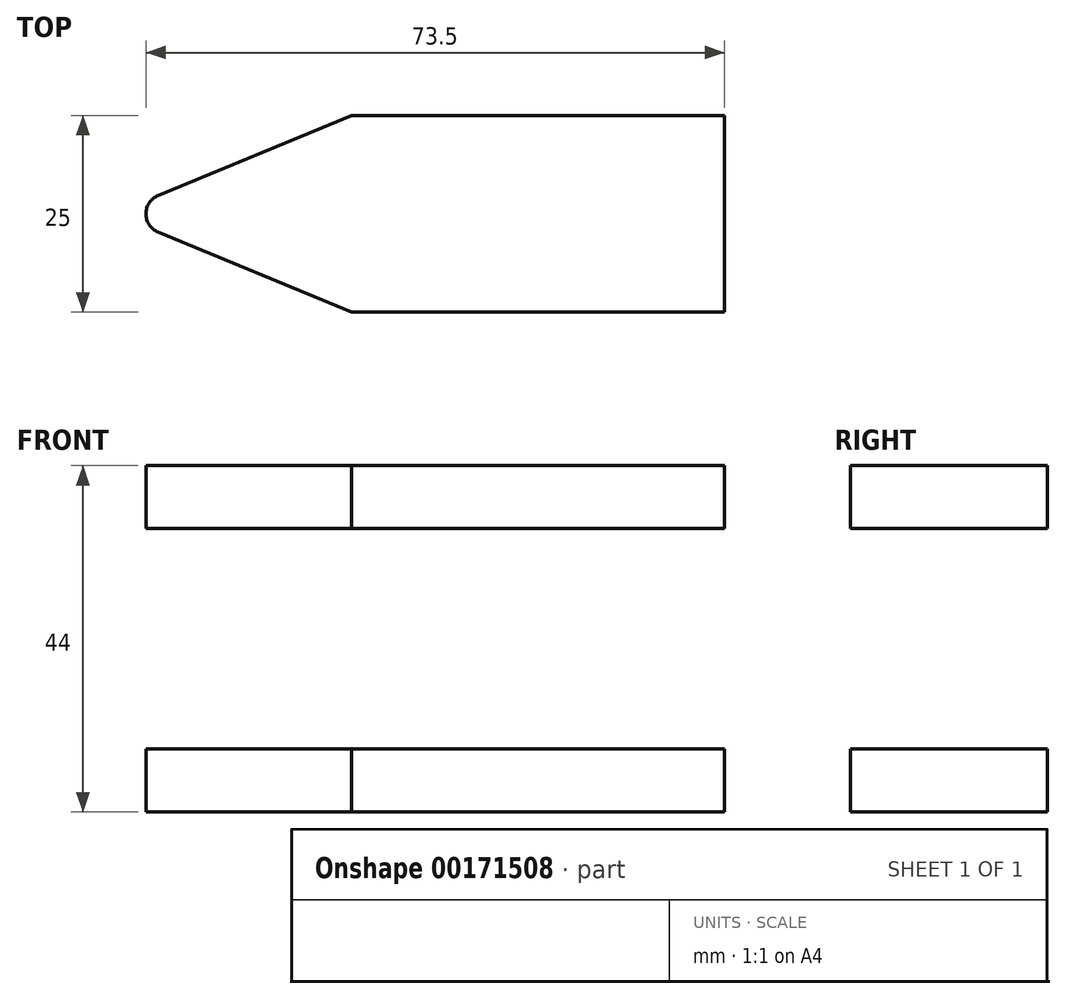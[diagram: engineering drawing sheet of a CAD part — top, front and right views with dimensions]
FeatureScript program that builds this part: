
annotation { "Feature Type Name" : "Feature", "Feature Type Description" : "" }
export const myFeature = defineFeature(function(context is Context, id is Id, definition is map)
    precondition{}
    {
        {
            var Q0;
            Q0=qCreatedBy(makeId("Front.planeOp"),FACE);
            var sketch = newSketch(context, id + "F0", { "sketchPlane" : qUnion([Q0])});
            skLineSegment(sketch, "E0", {"start": v(0, 14.3) * mm, "end": v(0, 0) * mm, "construction": true});
            skLineSegment(sketch, "E1", {"start": v(0, -14.1) * mm, "end": v(0, 0) * mm, "construction": true});
            skLineSegment(sketch, "E2", {"start": v(0, 0) * mm, "end": v(-25, 0) * mm, "construction": true});
            skLineSegment(sketch, "E3", {"start": v(-25, 0) * mm, "end": v(-25, 12.5) * mm, "construction": true});
            skLineSegment(sketch, "E4", {"start": v(-25, 12.5) * mm, "end": v(-23.5, 12.5) * mm, "construction": true});
            skLineSegment(sketch, "E5", {"start": v(-23.5, 12.5) * mm, "end": v(-23.5, 1.5) * mm, "construction": true});
            skLineSegment(sketch, "E6", {"start": v(-23.5, 1.5) * mm, "end": v(-1.5, 1.5) * mm, "construction": true});
            skLineSegment(sketch, "E7", {"start": v(-1.5, 1.5) * mm, "end": v(-1.5, 12.5) * mm, "construction": true});
            skLineSegment(sketch, "E8", {"start": v(-1.5, 12.5) * mm, "end": v(0, 12.5) * mm, "construction": true});
            skLineSegment(sketch, "E9", {"start": v(-23.5, 1.5) * mm, "end": v(-23.5, 0) * mm, "construction": true});
            skLineSegment(sketch, "E10.MirrorCS", {"start": v(-25, 0) * mm, "end": v(-25, -12.5) * mm, "construction": true});
            skLineSegment(sketch, "E11.MirrorCS", {"start": v(-25, -12.5) * mm, "end": v(-23.5, -12.5) * mm, "construction": true});
            skLineSegment(sketch, "E12.MirrorCS", {"start": v(-23.5, -12.5) * mm, "end": v(-23.5, -1.5) * mm, "construction": true});
            skLineSegment(sketch, "E13.MirrorCS", {"start": v(-23.5, -1.5) * mm, "end": v(-1.5, -1.5) * mm, "construction": true});
            skLineSegment(sketch, "E14.MirrorCS", {"start": v(-1.5, -1.5) * mm, "end": v(-1.5, -12.5) * mm, "construction": true});
            skLineSegment(sketch, "E15.MirrorCS", {"start": v(-1.5, -12.5) * mm, "end": v(0, -12.5) * mm, "construction": true});
            skSolve(sketch);
        }
        {
            var Q0;
            Q0=qCreatedBy(makeId("Front.planeOp"),FACE);
            var sketch = newSketch(context, id + "F1", { "sketchPlane" : qUnion([Q0])});
            skLineSegment(sketch, "E16.bottom", {"start": v(0, 0) * mm, "end": v(-12.5, 0) * mm, "construction": true});
            skLineSegment(sketch, "E16.top", {"start": v(0, 25) * mm, "end": v(-12.5, 25) * mm, "construction": true});
            skLineSegment(sketch, "E16.left", {"start": v(0, 0) * mm, "end": v(0, 1.5) * mm, "construction": true});
            skLineSegment(sketch, "E16.right", {"start": v(-12.5, 0) * mm, "end": v(-12.5, 25) * mm, "construction": true});
            skLineSegment(sketch, "E17.bottom", {"start": v(0, 23.5) * mm, "end": v(-11, 23.5) * mm, "construction": true});
            skLineSegment(sketch, "E17.top", {"start": v(0, 1.5) * mm, "end": v(-11, 1.5) * mm, "construction": true});
            skLineSegment(sketch, "E17.right", {"start": v(-11, 23.5) * mm, "end": v(-11, 1.5) * mm, "construction": true});
            skLineSegment(sketch, "E18", {"start": v(0, 0) * mm, "end": v(8.92, 0) * mm, "construction": true});
            skLineSegment(sketch, "E19.trimOffspring", {"start": v(0, 23.5) * mm, "end": v(0, 25) * mm, "construction": true});
            skLineSegment(sketch, "E20", {"start": v(-12.5, 23.5) * mm, "end": v(-11, 23.5) * mm, "construction": true});
            skLineSegment(sketch, "E21.MirrorCS", {"start": v(0, -23.5) * mm, "end": v(0, -25) * mm, "construction": true});
            skLineSegment(sketch, "E22.MirrorCS", {"start": v(0, 0) * mm, "end": v(0, -1.5) * mm, "construction": true});
            skLineSegment(sketch, "E23.MirrorCS", {"start": v(-12.5, -23.5) * mm, "end": v(-11, -23.5) * mm, "construction": true});
            skLineSegment(sketch, "E24.MirrorCS", {"start": v(-12.5, 0) * mm, "end": v(-12.5, -25) * mm, "construction": true});
            skLineSegment(sketch, "E25.MirrorCS", {"start": v(-11, -23.5) * mm, "end": v(-11, -1.5) * mm, "construction": true});
            skLineSegment(sketch, "E26.MirrorCS", {"start": v(0, -23.5) * mm, "end": v(-11, -23.5) * mm, "construction": true});
            skLineSegment(sketch, "E27.MirrorCS", {"start": v(0, -25) * mm, "end": v(-12.5, -25) * mm, "construction": true});
            skLineSegment(sketch, "E28.MirrorCS", {"start": v(0, -1.5) * mm, "end": v(-11, -1.5) * mm, "construction": true});
            skSolve(sketch);
        }
        {
            var Q0;
            Q0=qCreatedBy(makeId("Front.planeOp"),FACE);
            var sketch = newSketch(context, id + "F2", { "sketchPlane" : qUnion([Q0])});
            skLineSegment(sketch, "E29.bottom", {"start": v(-23.5, 22) * mm, "end": v(50, 22) * mm});
            skLineSegment(sketch, "E29.top", {"start": v(-23.5, 14) * mm, "end": v(50, 14) * mm});
            skLineSegment(sketch, "E29.left", {"start": v(-23.5, 22) * mm, "end": v(-23.5, 14) * mm});
            skLineSegment(sketch, "E29.right", {"start": v(50, 22) * mm, "end": v(50, 14) * mm});
            skLineSegment(sketch, "E30", {"start": v(-23.5, 18) * mm, "end": v(-13.83, 18) * mm, "construction": true});
            skPoint(sketch, "E30.endSnap0", {"position": v(-23.5, 18) * mm});
            skPoint(sketch, "E31.MirrorP", {"position": v(-23.5, -18) * mm});
            skLineSegment(sketch, "E32.MirrorCS", {"start": v(-23.5, -22) * mm, "end": v(50, -22) * mm});
            skLineSegment(sketch, "E33.MirrorCS", {"start": v(-23.5, -14) * mm, "end": v(50, -14) * mm});
            skLineSegment(sketch, "E34.MirrorCS", {"start": v(-23.5, -22) * mm, "end": v(-23.5, -14) * mm});
            skLineSegment(sketch, "E35.MirrorCS", {"start": v(50, -22) * mm, "end": v(50, -14) * mm});
            skSolve(sketch);
        }
        {
            var Q0;
            Q0=makeQuery(id+"F2.imprint","IMPRINT",FACE,{"disambiguationData":[TD([[makeQuery(id+"F2.imprint","IMPRINT",EDGE,{"derivedFrom":sQuery(id+"F2.wireOp",EDGE,"E29.bottom")}),-1.0]])]});
            extrude(context, id + "F3", {"entities" : qUnion([Q0]), "depth" : 12.5 * mm, "hasSecondDirection" : true, "secondDirectionOppositeDirection" : true, "secondDirectionDepth" : 12.5 * mm});
        }
        {
            var Q0;
            Q0=makeQuery(id+"F2.imprint","IMPRINT",FACE,{"disambiguationData":[TD([[makeQuery(id+"F2.imprint","IMPRINT",EDGE,{"derivedFrom":sQuery(id+"F2.wireOp",EDGE,"E32.MirrorCS")}),1.0]])]});
            extrude(context, id + "F4", {"entities" : qUnion([Q0]), "depth" : 12.5 * mm, "hasSecondDirection" : true, "secondDirectionOppositeDirection" : true, "secondDirectionDepth" : 12.5 * mm});
        }
        {
            var Q0;
            Q0=makeQuery(id+"F3.opExtrude","SWEPT_FACE",FACE,{"disambiguationData":[OSD([sQuery(id+"F2.wireOp",EDGE,"E29.bottom")])]});
            var sketch = newSketch(context, id + "F5", { "sketchPlane" : qUnion([Q0])});
            skArc(sketch, "E36", {"start": v(-21.96, 2.3) * mm, "mid": v(-23.5, 0) * mm, "end": v(-21.96, -2.3) * mm});
            skPoint(sketch, "E36.centerSnap0", {"position": v(-23.5, 0) * mm});
            skLineSegment(sketch, "E37", {"start": v(-21.96, 2.3) * mm, "end": v(2.64, 12.5) * mm});
            skLineSegment(sketch, "E38", {"start": v(2.64, -12.5) * mm, "end": v(-21.96, -2.3) * mm});
            skLineSegment(sketch, "E39", {"start": v(-23.5, 0) * mm, "end": v(-23.5, 12.5) * mm});
            skLineSegment(sketch, "E40", {"start": v(-23.5, 12.5) * mm, "end": v(2.64, 12.5) * mm});
            skLineSegment(sketch, "E41", {"start": v(2.64, -12.5) * mm, "end": v(-23.5, -12.5) * mm});
            skPoint(sketch, "E41.startSnap0", {"position": v(2.64, -12.5) * mm});
            skLineSegment(sketch, "E42", {"start": v(-23.5, -12.5) * mm, "end": v(-23.5, 0) * mm});
            skSolve(sketch);
        }
        {
            var Q0;
            {var subQ0=sQuery(id+"F5.wireOp",EDGE,"E37");Q0=makeQuery(id+"F5.imprint","IMPRINT",FACE,{"disambiguationData":[TD([[makeQuery(id+"F5.imprint","IMPRINT",EDGE,{"derivedFrom":subQ0}),1.0]])]});}
            var Q1;
            {var subQ0=sQuery(id+"F5.wireOp",EDGE,"E38");Q1=makeQuery(id+"F5.imprint","IMPRINT",FACE,{"disambiguationData":[TD([[makeQuery(id+"F5.imprint","IMPRINT",EDGE,{"derivedFrom":subQ0}),1.0]])]});}
            extrude(context, id + "F6", {"entities" : qUnion([Q0, Q1]), "operationType" : NewBodyOperationType.REMOVE, "endBound" : BoundingType.THROUGH_ALL, "oppositeDirection" : true, "depth" : 25 * mm});
        }
    });
